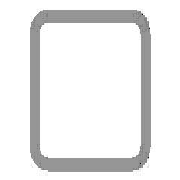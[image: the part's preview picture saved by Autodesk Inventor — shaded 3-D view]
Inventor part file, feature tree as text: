
AUTODESK INVENTOR PART (.ipt)
format: ipt  version: 2024 (Build 280153000, 153)  size: 150,016 bytes
history: native  units: mm (DEFAULTED — no unit token found)
features: other x4, plane x3, split x2, extrude x1, sketch x1
ambient origin geometry x8: Origin, YZ Plane, XZ Plane, XY Plane, X Axis, Y Axis, Z Axis, Center Point
bodies: Solid1 (feature_tree)
feature tree (11):
  parser-record x1  (decoder bookkeeping rows leaked as tree rows — omitted from the tree; the rows remain in map.json)
  other  "Driven Length"
  other  "Plano inicial"
  other  "Plano final"
  extrude  "Cuerpo"  TaperAngle=0.0deg  [1 undecoded]
  plane  "Plano de trabajo4"
  split  "Dividir1"
  plane  "Plano de trabajo5"
  split  "Dividir2"
  sketch  "Sketch3"  dims[d3=3050.8mm d4=0.0mm d10=50.8mm d11=50.8mm d12=3.175mm d13=-25.4mm d14=3025.4mm d15=25.4mm d16=25.4mm d17=6.35mm d18=90.0deg d19=3050.8mm]
  plane  "Work Plane3"
note: 1 required parameter value undecoded (feature->parameter linkage not recoverable at this tier; creation-order binding heuristic only, values carry confidence <= 0.55)
